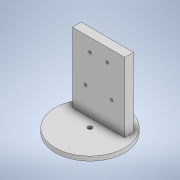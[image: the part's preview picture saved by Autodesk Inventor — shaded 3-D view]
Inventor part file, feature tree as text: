
AUTODESK INVENTOR PART (.ipt)
format: ipt  version: 2022 (Build 260153000, 153)  size: 127,488 bytes
history: native  units: mm
features: sketch x4, extrude x3
ambient origin geometry x8: Origin, YZ Plane, XZ Plane, XY Plane, X Axis, Y Axis, Z Axis, Center Point
bodies: Solid1 (feature_tree)
feature tree (7):
  extrude  "Extrusion1"  Depth=5.0mm
  extrude  "Extrusion2"  Depth=5.0mm
  extrude  "Extrusion3"  Depth=80.0mm TaperAngle=0.0deg
  sketch  "Sketch4"  dims[d13=3.0mm d14=3.0mm d18=3.0mm d19=3.0mm d20=5.0mm d21=0.0mm]
  sketch  "Sketch1"  dims[d0=80.0mm d1=5.0mm]
  sketch  "Sketch2"  dims[d2=5.0mm d3=0.0mm d5=30.0mm]
  sketch  "Sketch3"  dims[d6=10.0mm d8=80.0mm d9=0.0mm]
